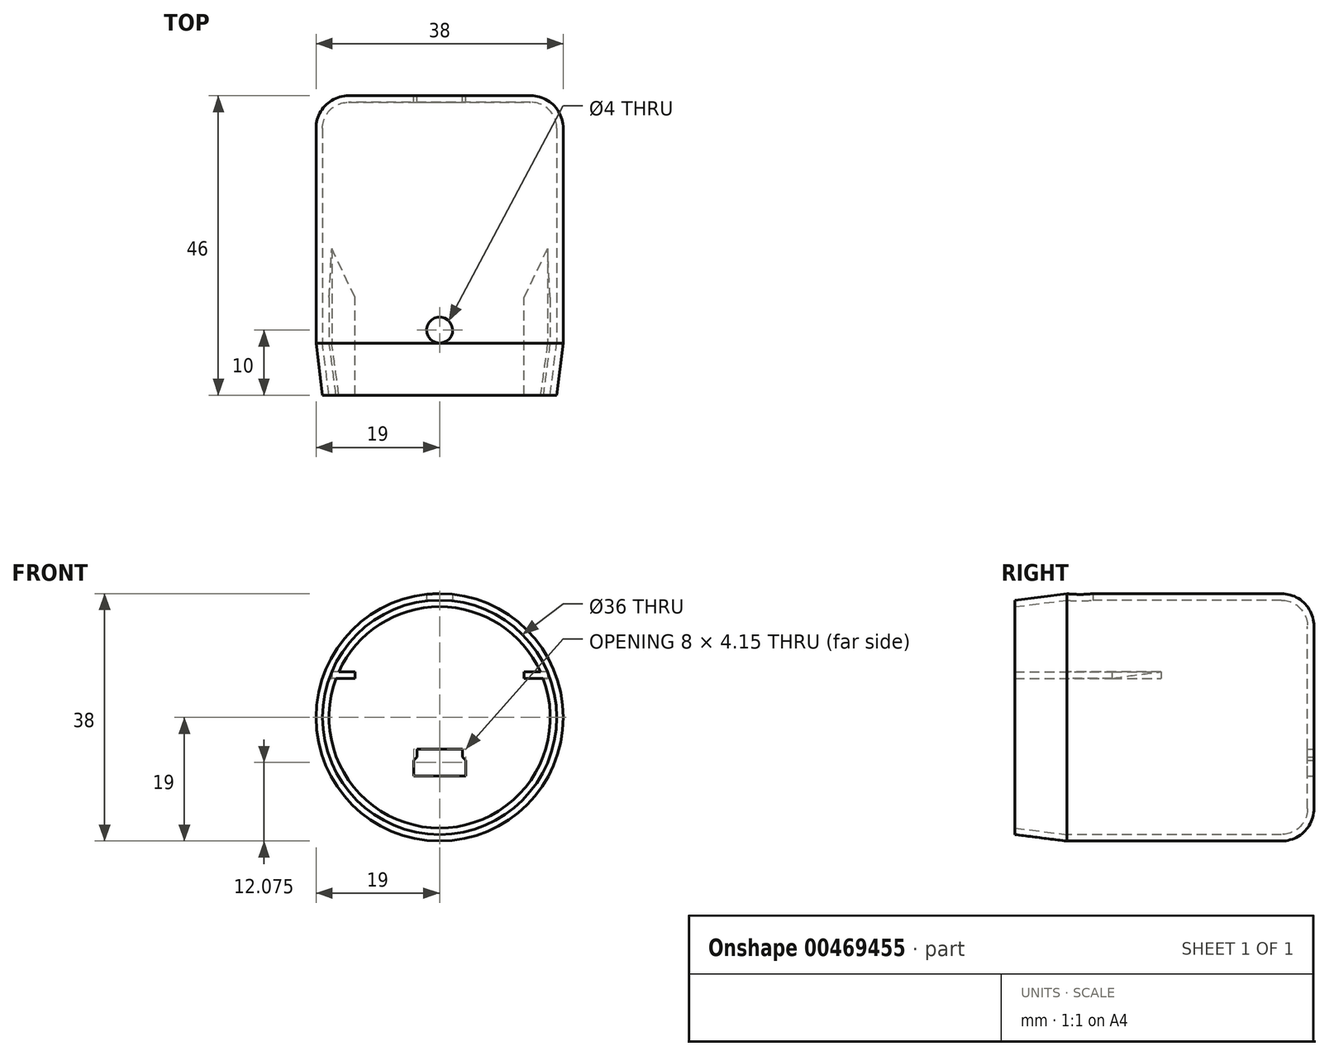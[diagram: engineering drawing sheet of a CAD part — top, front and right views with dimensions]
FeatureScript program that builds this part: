
annotation { "Feature Type Name" : "Feature", "Feature Type Description" : "" }
export const myFeature = defineFeature(function(context is Context, id is Id, definition is map)
    precondition{}
    {
        {
            var Q0;
            Q0=qCreatedBy(makeId("Right.planeOp"),FACE);
            var sketch = newSketch(context, id + "F0", { "sketchPlane" : qUnion([Q0])});
            skLineSegment(sketch, "E0", {"start": v(-97.63, 0) * mm, "end": v(101.73, 0) * mm});
            skLineSegment(sketch, "E1", {"start": v(-18, 18) * mm, "end": v(-10, 19) * mm});
            skLineSegment(sketch, "E2", {"start": v(-10, 19) * mm, "end": v(23, 19) * mm});
            skLineSegment(sketch, "E3", {"start": v(-18, 17) * mm, "end": v(-10, 18) * mm});
            skLineSegment(sketch, "E4", {"start": v(-10, 18) * mm, "end": v(23, 18) * mm});
            skLineSegment(sketch, "E5", {"start": v(-18, 18) * mm, "end": v(-18, 17) * mm});
            skLineSegment(sketch, "E6", {"start": v(28, 0) * mm, "end": v(28, 14) * mm});
            skArc(sketch, "E7", {"start": v(28, 14) * mm, "mid": v(26.54, 17.54) * mm, "end": v(23, 19) * mm});
            skArc(sketch, "E8.0", {"start": v(27, 14) * mm, "mid": v(25.83, 16.83) * mm, "end": v(23, 18) * mm});
            skLineSegment(sketch, "E8.1", {"start": v(27, 0) * mm, "end": v(27, 14) * mm});
            skLineSegment(sketch, "E9.bottom", {"start": v(-18, 6) * mm, "end": v(-3, 6) * mm});
            skLineSegment(sketch, "E9.top", {"start": v(-18, 7) * mm, "end": v(-3, 7) * mm});
            skLineSegment(sketch, "E9.left", {"start": v(-18, 6) * mm, "end": v(-18, 7) * mm});
            skLineSegment(sketch, "E9.right", {"start": v(-3, 6) * mm, "end": v(-3, 7) * mm});
            skSolve(sketch);
        }
        {
            var Q0;
            Q0=makeQuery(id+"F0.imprint","IMPRINT",FACE,{"disambiguationData":[TD([[makeQuery(id+"F0.imprint","IMPRINT",EDGE,{"derivedFrom":sQuery(id+"F0.wireOp",EDGE,"E1")}),-1.0]])]});
            var Q1;
            Q1=sQuery(id+"F0.wireOp",EDGE,"E0");
            revolve(context, id + "F1", {"entities" : qUnion([Q0]), "axis" : qUnion([Q1]), "revolveType" : RevolveType.FULL});
        }
        {
            var Q0;
            Q0=makeQuery(id+"F1.opRevolve","SWEPT_FACE",FACE,{"disambiguationData":[OSD([sQuery(id+"F0.wireOp",EDGE,"E6")])]});
            var sketch = newSketch(context, id + "F2", { "sketchPlane" : qUnion([Q0])});
            skLineSegment(sketch, "E10", {"start": v(0, -4.85) * mm, "end": v(3.5, -4.85) * mm});
            skLineSegment(sketch, "E11", {"start": v(3.5, -4.85) * mm, "end": v(3.5, -6.1) * mm});
            skLineSegment(sketch, "E12", {"start": v(3.5, -6.1) * mm, "end": v(4, -6.6) * mm});
            skLineSegment(sketch, "E13", {"start": v(4, -6.6) * mm, "end": v(4, -9) * mm});
            skLineSegment(sketch, "E14", {"start": v(4, -9) * mm, "end": v(0, -9) * mm});
            skLineSegment(sketch, "E15.MirrorCS", {"start": v(-3.5, -6.1) * mm, "end": v(-4, -6.6) * mm});
            skLineSegment(sketch, "E16.MirrorCS", {"start": v(0, -4.85) * mm, "end": v(-3.5, -4.85) * mm});
            skLineSegment(sketch, "E17.MirrorCS", {"start": v(-3.5, -4.85) * mm, "end": v(-3.5, -6.1) * mm});
            skLineSegment(sketch, "E18.MirrorCS", {"start": v(-4, -9) * mm, "end": v(0, -9) * mm});
            skLineSegment(sketch, "E19.MirrorCS", {"start": v(-4, -6.6) * mm, "end": v(-4, -9) * mm});
            skSolve(sketch);
        }
        {
            var Q0;
            Q0=makeQuery(id+"F2.imprint","IMPRINT",FACE,{"disambiguationData":[TD([[makeQuery(id+"F2.imprint","IMPRINT",EDGE,{"derivedFrom":sQuery(id+"F2.wireOp",EDGE,"E10")}),-1.0]])]});
            extrude(context, id + "F3", {"entities" : qUnion([Q0]), "operationType" : NewBodyOperationType.REMOVE, "oppositeDirection" : true, "depth" : 2 * mm, "offsetDistance" : 25 * mm});
        }
        {
            var Q0;
            Q0=makeQuery(id+"F0.imprint","IMPRINT",FACE,{"disambiguationData":[TD([[makeQuery(id+"F0.imprint","IMPRINT",EDGE,{"derivedFrom":sQuery(id+"F0.wireOp",EDGE,"E9.bottom")}),1.0]])]});
            var Q1;
            Q1=makeQuery(id+"F1.opRevolve","SWEPT_FACE",FACE,{"disambiguationData":[OSD([sQuery(id+"F0.wireOp",EDGE,"E4")])]});
            var Q2;
            Q2=makeQuery(id+"F1.opRevolve","SWEPT_FACE",FACE,{"disambiguationData":[OSD([sQuery(id+"F0.wireOp",EDGE,"E4")])]});
            extrude(context, id + "F4", {"entities" : qUnion([Q0]), "operationType" : NewBodyOperationType.ADD, "endBound" : BoundingType.UP_TO_SURFACE, "depth" : 25 * mm, "endBoundEntityFace" : qUnion([Q1]), "offsetDistance" : 25 * mm, "hasSecondDirection" : true, "secondDirectionBound" : SecondDirectionBoundingType.UP_TO_SURFACE, "secondDirectionOppositeDirection" : true, "secondDirectionDepth" : 25 * mm, "secondDirectionBoundEntityFace" : qUnion([Q2])});
        }
        {
            var Q0;
            Q0=makeQuery(id+"F0.imprint","IMPRINT",FACE,{"disambiguationData":[TD([[makeQuery(id+"F0.imprint","IMPRINT",EDGE,{"derivedFrom":sQuery(id+"F0.wireOp",EDGE,"E9.bottom")}),1.0]])]});
            extrude(context, id + "F5", {"entities" : qUnion([Q0]), "operationType" : NewBodyOperationType.REMOVE, "oppositeDirection" : true, "depth" : 13 * mm, "offsetDistance" : 25 * mm, "hasSecondDirection" : true, "secondDirectionOppositeDirection" : false, "secondDirectionDepth" : 13 * mm});
        }
        {
            var Q0;
            {var subQ0=sQuery(id+"F0.wireOp",EDGE,"E9.left");var subQ1=sQuery(id+"F0.wireOp",EDGE,"E9.right");var subQ2=sQuery(id+"F0.wireOp",EDGE,"E9.bottom");Q0=makeQuery(id+"F5.boolean.opBoolean","SPLIT",FACE,{"disambiguationData":[TD([makeQuery(id+"F5.opExtrude","CAP_FACE",FACE,{"disambiguationData":[OSD([subQ2,sQuery(id+"F0.wireOp",EDGE,"E9.top"),subQ0,subQ1])],"isStart":true})])],"derivedFrom":makeQuery(id+"F4.opExtrude","SWEPT_FACE",FACE,{"disambiguationData":[OSD([subQ2])]})});}
            var sketch = newSketch(context, id + "F6", { "sketchPlane" : qUnion([Q0])});
            skLineSegment(sketch, "E20", {"start": v(13, 3) * mm, "end": v(16.58, -4.5) * mm});
            skLineSegment(sketch, "E21", {"start": v(16.97, 3) * mm, "end": v(16.58, -4.5) * mm});
            skLineSegment(sketch, "E22", {"start": v(13, 3) * mm, "end": v(16.97, 3) * mm});
            skLineSegment(sketch, "E23.MirrorCS", {"start": v(-13, 3) * mm, "end": v(-16.58, -4.5) * mm});
            skLineSegment(sketch, "E24.MirrorCS", {"start": v(-13, 3) * mm, "end": v(-16.97, 3) * mm});
            skLineSegment(sketch, "E25.MirrorCS", {"start": v(-16.97, 3) * mm, "end": v(-16.58, -4.5) * mm});
            skSolve(sketch);
        }
        {
            var Q0;
            Q0=makeQuery(id+"F6.imprint","IMPRINT",FACE,{"disambiguationData":[TD([[makeQuery(id+"F6.imprint","IMPRINT",EDGE,{"derivedFrom":sQuery(id+"F6.wireOp",EDGE,"E23.MirrorCS")}),-1.0]])]});
            var Q1;
            Q1=makeQuery(id+"F6.imprint","IMPRINT",FACE,{"disambiguationData":[TD([[makeQuery(id+"F6.imprint","IMPRINT",EDGE,{"derivedFrom":sQuery(id+"F6.wireOp",EDGE,"E20")}),1.0]])]});
            extrude(context, id + "F7", {"entities" : qUnion([Q0, Q1]), "operationType" : NewBodyOperationType.ADD, "oppositeDirection" : true, "depth" : 1 * mm, "offsetDistance" : 25 * mm});
        }
        {
            var Q0;
            Q0=qCreatedBy(makeId("Top.planeOp"),FACE);
            var sketch = newSketch(context, id + "F8", { "sketchPlane" : qUnion([Q0])});
            skPoint(sketch, "E26", {"position": v(0, -8) * mm});
            skSolve(sketch);
        }
        {
            var Q0;
            Q0=sQuery(id+"F8.wireOp",VERTEX,"E26");
            var Q1;
            Q1=makeQuery(id+"F1.opRevolve","SWEPT_BODY",BODY,{"disambiguationData":[OSD([sQuery(id+"F0.wireOp",EDGE,"E0"),sQuery(id+"F0.wireOp",EDGE,"E1"),sQuery(id+"F0.wireOp",EDGE,"E2"),sQuery(id+"F0.wireOp",EDGE,"E3"),sQuery(id+"F0.wireOp",EDGE,"E4"),sQuery(id+"F0.wireOp",EDGE,"E5"),sQuery(id+"F0.wireOp",EDGE,"E6"),sQuery(id+"F0.wireOp",EDGE,"E7"),sQuery(id+"F0.wireOp",EDGE,"E8.0"),sQuery(id+"F0.wireOp",EDGE,"E8.1")])]});
            hole(context, id + "F9", {"style" : HoleStyle.SIMPLE, "endStyle" : HoleEndStyle.THROUGH, "oppositeDirection" : true, "holeDiameter" : 4 * mm, "isTappedThrough" : true, "tappedDepth" : 12 * mm, "tapClearance" : 3, "locations" : qUnion([Q0]), "scope" : qUnion([Q1])});
        }
    });
